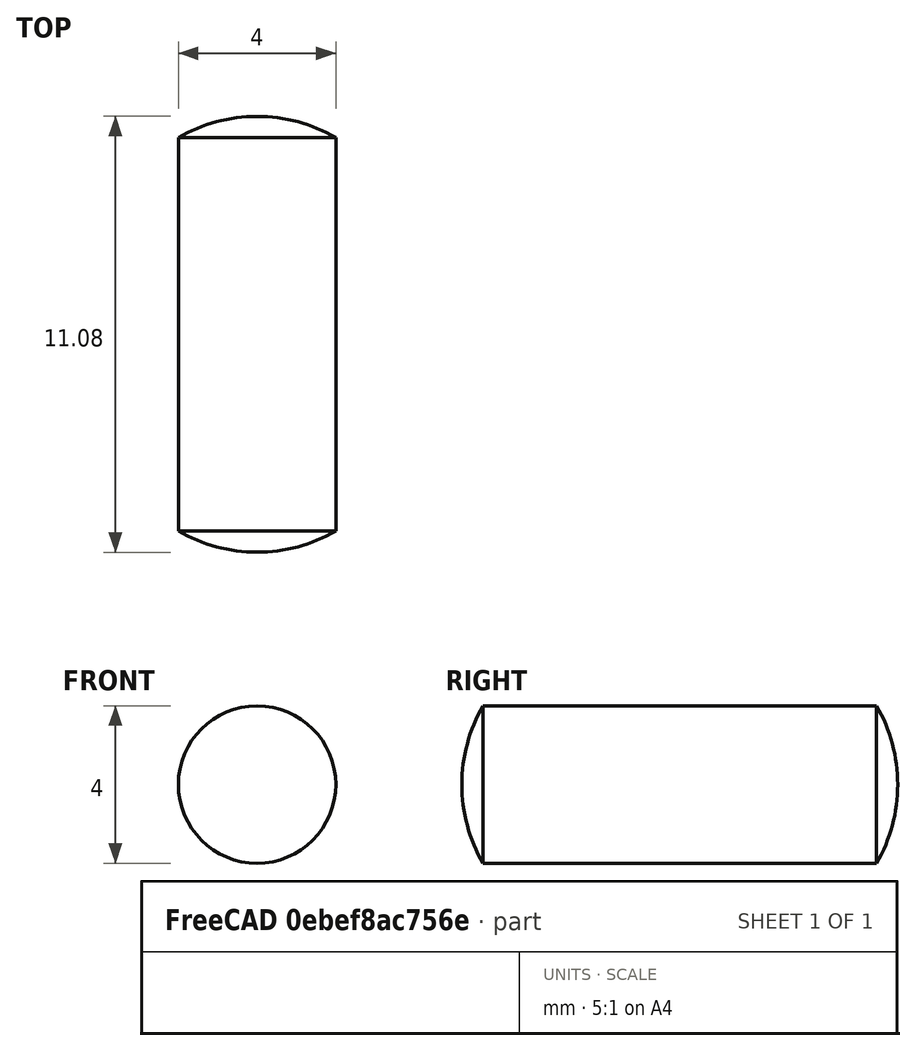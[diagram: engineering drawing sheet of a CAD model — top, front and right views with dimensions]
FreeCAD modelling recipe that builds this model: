
FCSTD DOCUMENT  (FreeCAD 0.15R4470 (Git))
Label: Zyl-Stift_DIN_7-4x10
License: CC-BY 3.0
LicenseURL: http://creativecommons.org/licenses/by/3.0/
objects: Sketcher::SketchObject×1, PartDesign::Revolution×1
note: 3 computed .brp shape members not serialized (recipe doc carries the construction recipe); baked Part::Feature solids carry a one-line shape summary decoded from their .brp

FEATURE [Sketcher::SketchObject] Sketch
  Placement = pos=(0,0,0) rot=(0.57735,0.57735,0.57735;2.0944rad)
  sketch-geometry (4):
    g0: ArcOfCircle CenterX=6.5359 CenterY=0 CenterZ=0 NormalX=0 NormalY=0 NormalZ=1 Radius=4 StartAngle=0 EndAngle=0.523599
    g1: LineSegment StartX=0 StartY=2 StartZ=0 EndX=10 EndY=2 EndZ=0
    g2: LineSegment StartX=-0.535898 StartY=0 StartZ=0 EndX=10.5359 EndY=0 EndZ=0
    g3: ArcOfCircle CenterX=3.4641 CenterY=0 CenterZ=0 NormalX=0 NormalY=0 NormalZ=1 Radius=4 StartAngle=2.61799 EndAngle=3.14159
  constraints (14):
    c: PointOnObject(g2,g-1)
    c: PointOnObject(g1,g-2)
    c: Coincident(g0,g1)
    c: PointOnObject(g0,g-1)
    c: Horizontal(g1)
    c: Coincident(g2,g0)
    c: Horizontal(g2)
    c: Radius(g0) = 4
    c: PointOnObject(g3,g2)
    c: Coincident(g3,g1)
    c: Coincident(g3,g2)
    c: Equal(g3,g0)
    c: DistanceY(g-1,g1) = 2
    c: DistanceX(g1) = 10
FEATURE [PartDesign::Revolution] Revolution  label="Zyl-Stift DIN 7-4x10 #"
  Angle = 360
  Axis = (0,1,0)
  Base = (0,0,0)
  Placement = pos=(0,0,0) rot=(0.57735,0.57735,0.57735;2.0944rad)
  ReferenceAxis = -> Sketch [H_Axis]
  Sketch = -> Sketch
